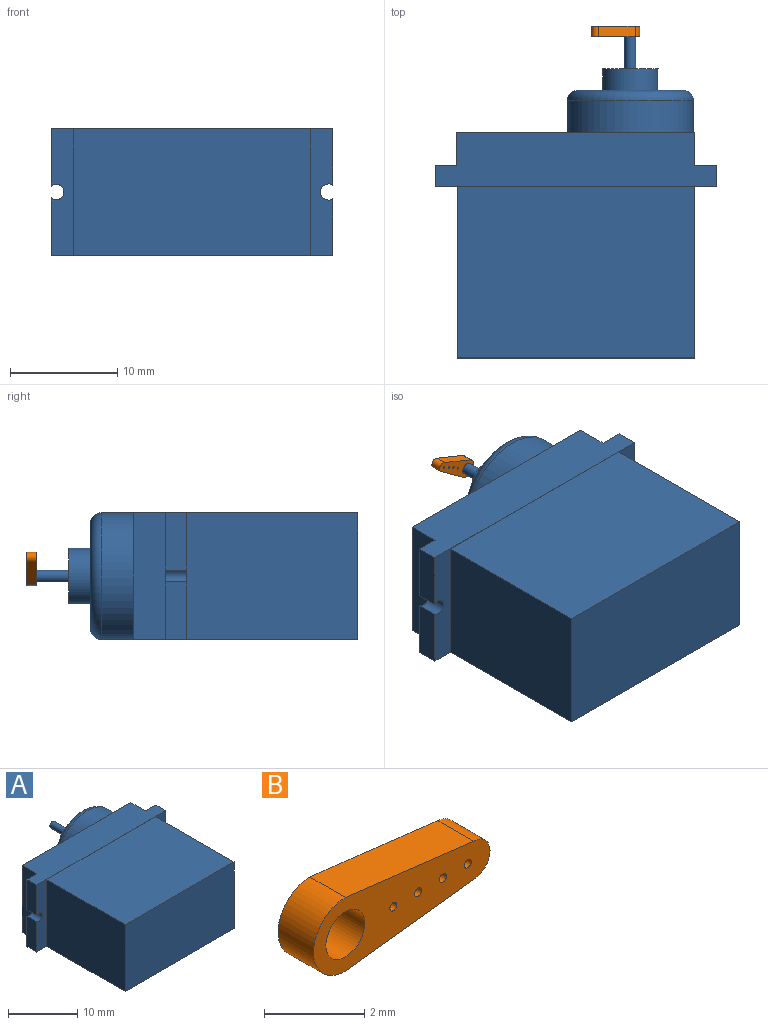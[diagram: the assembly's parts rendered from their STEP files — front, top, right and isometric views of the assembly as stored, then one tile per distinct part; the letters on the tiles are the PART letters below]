
ASSEMBLY  parts=2 mates=1
PART A: 25 faces, bbox 26.3x31x12.8 mm
  f0: plane 11.82x2.1mm, normal (0,1,0), area 23.4mm2, adj f3,f8,f9,f10,f11,f16
  f1: plane 22.2x16mm, normal (0,0,1), area 355.2mm2, adj f2,f4,f5,f6
  f2: plane 16x11.8mm, normal (-1,0,0), area 188.8mm2, adj f1,f3,f5,f6
  f3: plane 26.32x24.15mm, normal (0,0,-1), area 476.6mm2, adj f0,f2,f4,f5,f6,f7,f8,f14
  f4: plane 16x11.8mm, normal (1,0,0), area 188.8mm2, adj f1,f3,f5,f6
  f5: plane 22.2x11.8mm, normal (0,-1,0), area 262mm2, adj f1,f2,f3,f4
  f6: plane 26.32x11.82mm, normal (0,-1,0), area 46.2mm2, adj f1,f2,f3,f4,f7,f8,f9,f10
  f7: plane 5.35x2mm, normal (-1,0,0), area 10.7mm2, adj f3,f6,f13,f14
  f8: plane 5.27x2mm, normal (1,0,0), area 10.5mm2, adj f0,f3,f6,f9
  f9: cylinder r=0.76mm len=2mm, axis (0,-1,0), area 6.5mm2, adj f0,f6,f8,f10
  f10: plane 5.27x2mm, normal (1,0,0), area 10.5mm2, adj f0,f6,f9,f11
  f11: plane 26.32x5mm, normal (0,0,1), area 119.2mm2, adj f0,f6,f10,f12,f14,f15,f16,f17
  f12: plane 5.35x2mm, normal (-1,0,0), area 10.7mm2, adj f6,f11,f13,f14
  f13: cylinder r=0.72mm len=2mm, axis (0,-1,0), area 6.5mm2, adj f6,f7,f12,f14
  f14: plane 11.82x2.01mm, normal (0,1,0), area 22.3mm2, adj f3,f7,f11,f12,f13,f15
  f15: plane 11.82x3mm, normal (-1,0,0), area 35.5mm2, adj f3,f11,f14,f17
  f16: plane 11.82x3mm, normal (1,0,0), area 35.5mm2, adj f0,f3,f11,f17
  f17: plane 22.2x11.82mm, normal (0,1,0), area 152.7mm2, adj f3,f11,f15,f16,f18
  f18: cylinder r=5.91mm len=11.82mm, axis (0,-1,0), area 109.3mm2, adj f3,f17,f20
  f19: plane 9.82x9.82mm, normal (0,1,0), area 54.7mm2, adj f20,f21
  f20: torus R=4.91mm, axis (0,1,0), area 54.7mm2, adj f3,f18,f19
  f21: cylinder r=2.59mm len=5.18mm, axis (0,-1,0), area 32.6mm2, adj f19,f22
  f22: plane 5.18x5.18mm, normal (0,1,0), area 20.1mm2, adj f21,f23
  f23: cylinder r=0.55mm len=4mm, axis (0,-1,0), area 13.8mm2, adj f22,f24
  f24: plane 1.1x1.1mm, normal (0,1,0), area 1mm2, adj f23
PART B: 11 faces, bbox 5x1x1.8 mm
  f0: plane 3.61x1mm, normal (0.12,0,-0.99), area 3.6mm2, adj f1,f8,f9,f10
  f1: cylinder r=0.47mm len=1mm, axis (0,1,0), area 1.5mm2, adj f0,f2,f9,f10
  f2: plane 3.61x1mm, normal (0.12,0,0.99), area 3.6mm2, adj f1,f8,f9,f10
  f3: cylinder r=0.55mm len=1.1mm, axis (0,1,0), area 3.5mm2, adj f9,f10
  f4: cylinder r=0.1mm len=1mm, axis (0,1,0), area 0.6mm2, adj f9,f10
  f5: cylinder r=0.1mm len=1mm, axis (0,1,0), area 0.6mm2, adj f9,f10
  f6: cylinder r=0.1mm len=1mm, axis (0,1,0), area 0.6mm2, adj f9,f10
  f7: cylinder r=0.1mm len=1mm, axis (0,1,0), area 0.6mm2, adj f9,f10
  f8: cylinder r=0.9mm len=1.8mm, axis (0,1,0), area 2.8mm2, adj f0,f2,f9,f10
  f9: plane 4.98x1.8mm, normal (0,-1,0), area 5.5mm2, adj f0,f1,f2,f3,f4,f5,f6,f7
  f10: plane 4.98x1.8mm, normal (0,1,0), area 5.5mm2, adj f0,f1,f2,f3,f4,f5,f6,f7
PLACE A t=(2.92,2.88,-4.67)mm fixed
PLACE B rot(axis=(0,-1,0),151.1deg) t=(-53.65,17.88,34.16)mm
MATE revolute B.f3 <-> A.f18  axis (0,1,0) through (-44.93,17.88,1.23)mm
